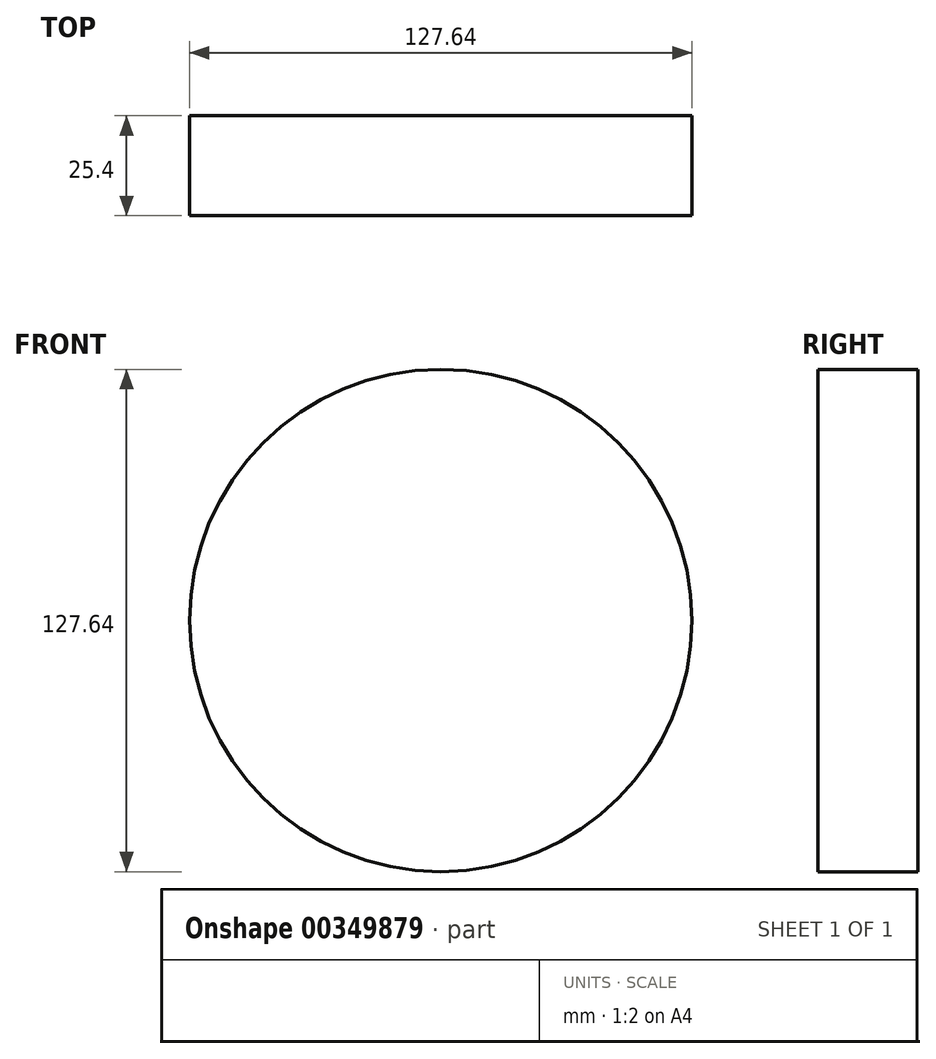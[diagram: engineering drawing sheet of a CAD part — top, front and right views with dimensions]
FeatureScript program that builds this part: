
annotation { "Feature Type Name" : "Feature", "Feature Type Description" : "" }
export const myFeature = defineFeature(function(context is Context, id is Id, definition is map)
    precondition{}
    {
        {
            var Q0;
            Q0=qCreatedBy(makeId("Front.planeOp"),FACE);
            var sketch = newSketch(context, id + "F0", { "sketchPlane" : qUnion([Q0])});
            skCircle(sketch, "E0", {"center": v(-0.14, 0.08) * mm, "radius": 63.82 * mm});
            skSolve(sketch);
        }
        {
            var Q0;
            Q0=makeQuery(id+"F0.imprint","IMPRINT",FACE,{"disambiguationData":[TD([[makeQuery(id+"F0.imprint","IMPRINT",EDGE,{"derivedFrom":sQuery(id+"F0.wireOp",EDGE,"E0")}),1.0]])]});
            var Q1;
            Q1=sQuery(id+"F0.wireOp",EDGE,"E0");
            extrude(context, id + "F1", {"entities" : qUnion([Q0]), "surfaceEntities" : qUnion([Q1]), "depth" : 25.4 * mm});
        }
    });
